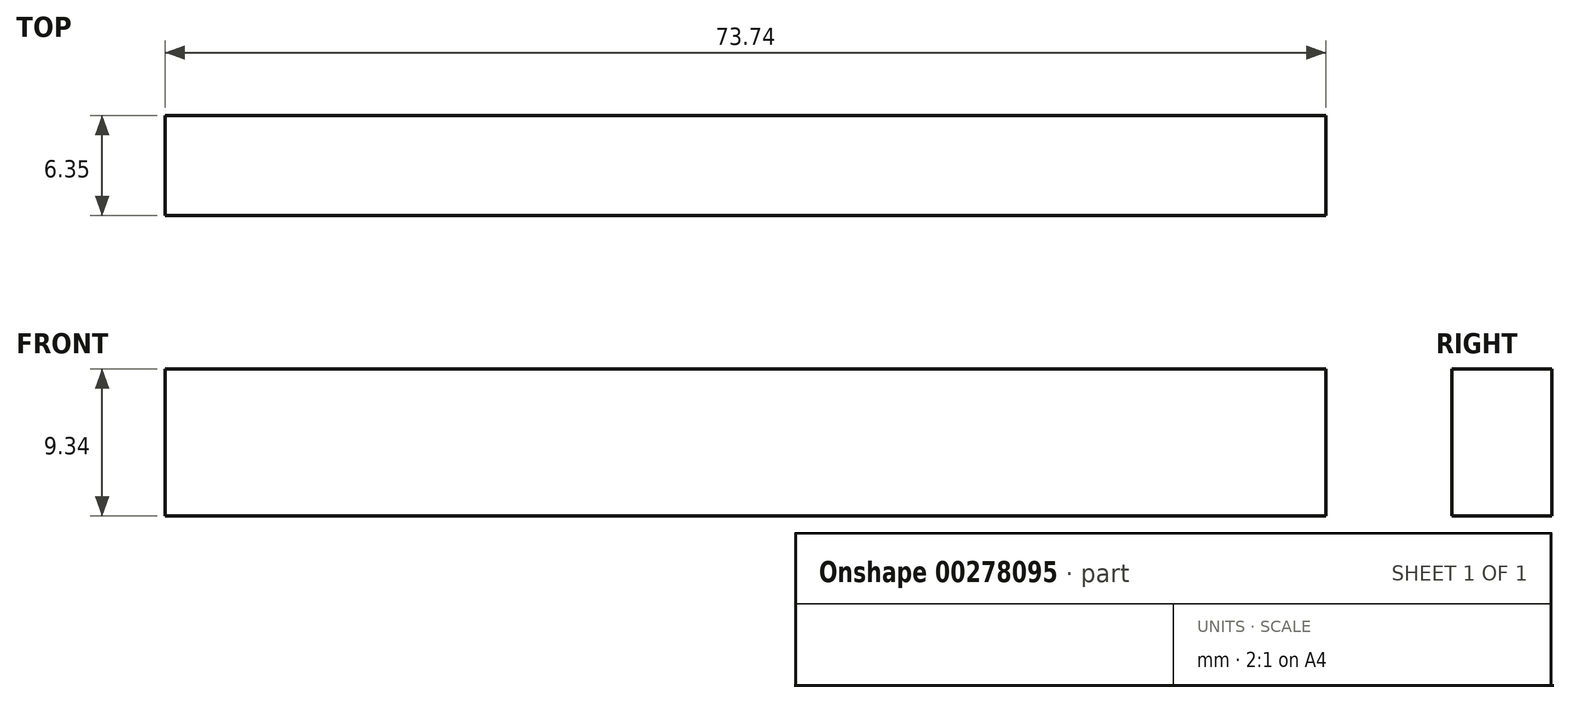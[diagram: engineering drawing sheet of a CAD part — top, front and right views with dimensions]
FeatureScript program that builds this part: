
annotation { "Feature Type Name" : "Feature", "Feature Type Description" : "" }
export const myFeature = defineFeature(function(context is Context, id is Id, definition is map)
    precondition{}
    {
        {
            var Q0;
            Q0=qCreatedBy(makeId("Front.planeOp"),FACE);
            var sketch = newSketch(context, id + "F0", { "sketchPlane" : qUnion([Q0])});
            skLineSegment(sketch, "E0.bottom", {"start": v(0, -2.41) * mm, "end": v(36.87, -2.41) * mm});
            skLineSegment(sketch, "E0.top", {"start": v(0, -11.75) * mm, "end": v(36.87, -11.75) * mm});
            skLineSegment(sketch, "E0.left", {"start": v(0, -2.41) * mm, "end": v(0, -11.75) * mm});
            skLineSegment(sketch, "E0.right", {"start": v(36.87, -2.41) * mm, "end": v(36.87, -11.75) * mm});
            skLineSegment(sketch, "E1.MirrorCS", {"start": v(-36.87, -2.41) * mm, "end": v(-36.87, -11.75) * mm});
            skLineSegment(sketch, "E2.MirrorCS", {"start": v(0, -2.41) * mm, "end": v(-36.87, -2.41) * mm});
            skLineSegment(sketch, "E3.MirrorCS", {"start": v(0, -11.75) * mm, "end": v(-36.87, -11.75) * mm});
            skSolve(sketch);
        }
        {
            var Q0;
            Q0=makeQuery(id+"F0.imprint","IMPRINT",FACE,{"disambiguationData":[TD([[makeQuery(id+"F0.imprint","IMPRINT",EDGE,{"derivedFrom":sQuery(id+"F0.wireOp",EDGE,"E0.bottom")}),-1.0]])]});
            var Q1;
            Q1=makeQuery(id+"F0.imprint","IMPRINT",FACE,{"disambiguationData":[TD([[makeQuery(id+"F0.imprint","IMPRINT",EDGE,{"derivedFrom":sQuery(id+"F0.wireOp",EDGE,"E0.left")}),-1.0]])]});
            extrude(context, id + "F1", {"entities" : qUnion([Q0, Q1]), "depth" : 6.35 * mm});
        }
    });
